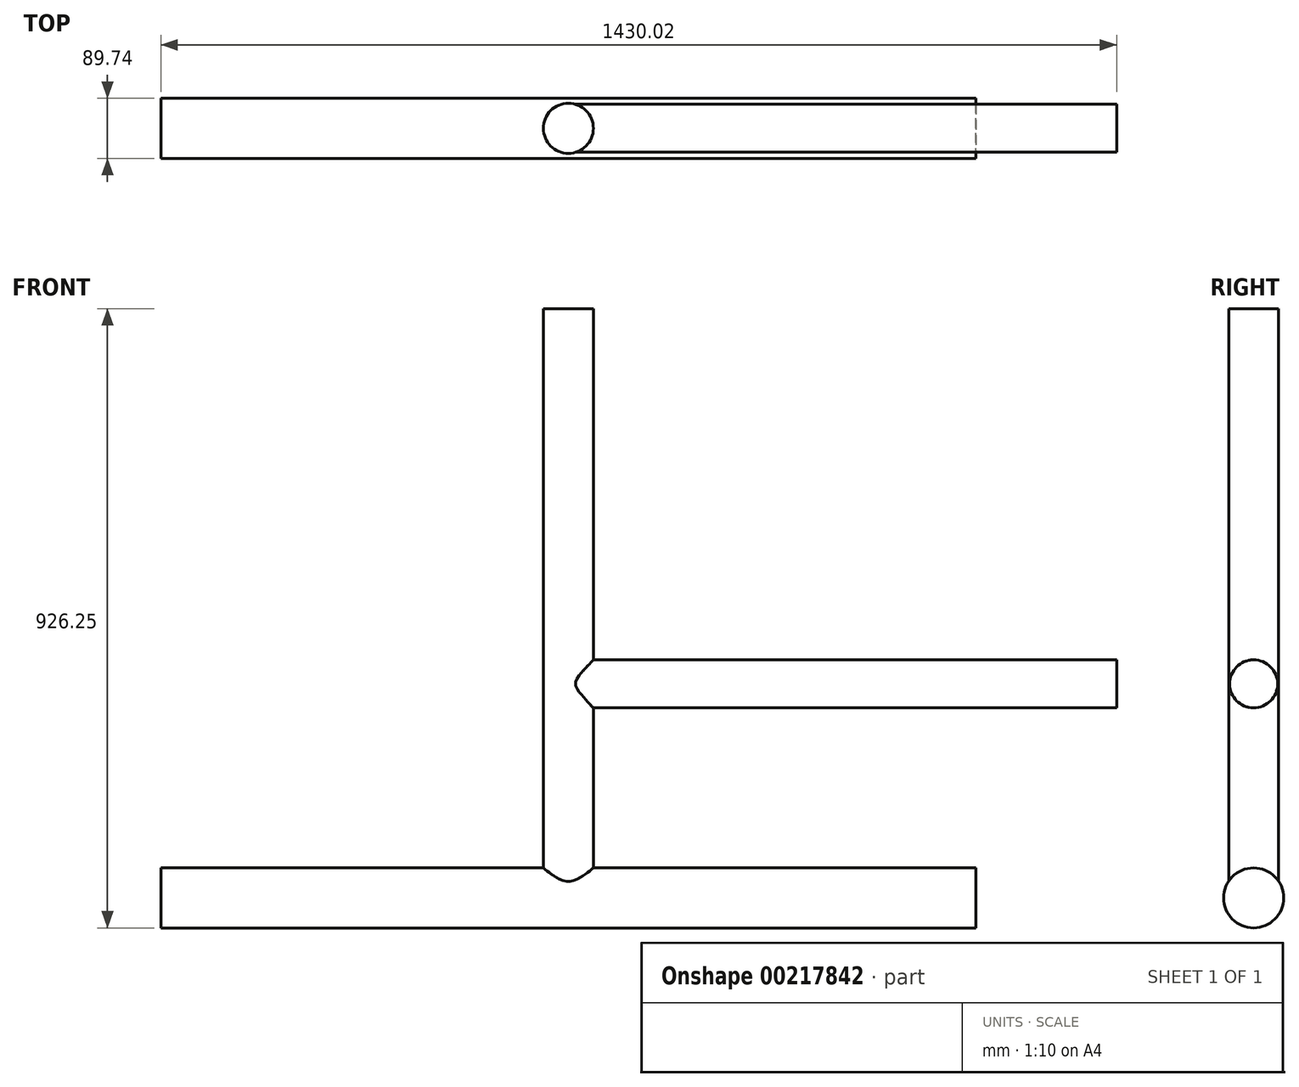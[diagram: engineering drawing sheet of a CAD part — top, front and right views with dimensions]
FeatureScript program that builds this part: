
annotation { "Feature Type Name" : "Feature", "Feature Type Description" : "" }
export const myFeature = defineFeature(function(context is Context, id is Id, definition is map)
    precondition{}
    {
        {
            var Q0;
            Q0=qCreatedBy(makeId("Top.planeOp"),FACE);
            var sketch = newSketch(context, id + "F0", { "sketchPlane" : qUnion([Q0])});
            skCircle(sketch, "E0", {"center": v(0, 0) * mm, "radius": 23.13 * mm});
            skSolve(sketch);
        }
        {
            var Q0;
            Q0 = qSketchRegion(id + "F0", true);
            extrude(context, id + "F1", {"entities" : qUnion([Q0]), "depth" : 711.2 * mm});
        }
        {
            var Q0;
            Q0=qCreatedBy(makeId("Right.planeOp"),FACE);
            var sketch = newSketch(context, id + "F2", { "sketchPlane" : qUnion([Q0])});
            skCircle(sketch, "E1", {"center": v(0, 0) * mm, "radius": 44.87 * mm});
            skSolve(sketch);
        }
        {
            var Q0;
            Q0 = qSketchRegion(id + "F2", true);
            extrude(context, id + "F3", {"entities" : qUnion([Q0]), "operationType" : NewBodyOperationType.ADD, "depth" : 609.6 * mm, "hasSecondDirection" : true, "secondDirectionOppositeDirection" : true, "secondDirectionDepth" : 609.6 * mm});
        }
        {
            var Q0;
            Q0=qCreatedBy(makeId("Top.planeOp"),FACE);
            var sketch = newSketch(context, id + "F4", { "sketchPlane" : qUnion([Q0])});
            skCircle(sketch, "E2", {"center": v(0, 0) * mm, "radius": 37.42 * mm});
            skSolve(sketch);
        }
        {
            var Q0;
            Q0 = qSketchRegion(id + "F4", true);
            extrude(context, id + "F5", {"entities" : qUnion([Q0]), "operationType" : NewBodyOperationType.ADD, "depth" : 881.38 * mm});
        }
        {
            var Q0;
            Q0=qCreatedBy(makeId("Right.planeOp"),FACE);
            var sketch = newSketch(context, id + "F6", { "sketchPlane" : qUnion([Q0])});
            skCircle(sketch, "E3", {"center": v(0, 0) * mm, "radius": 42.2 * mm});
            skSolve(sketch);
        }
        {
            var Q0;
            Q0 = qSketchRegion(id + "F6", true);
            extrude(context, id + "F7", {"entities" : qUnion([Q0]), "operationType" : NewBodyOperationType.ADD, "oppositeDirection" : true, "depth" : 43.18 * mm});
        }
        {
            var Q0;
            Q0=qCreatedBy(makeId("Right.planeOp"),FACE);
            var sketch = newSketch(context, id + "F8", { "sketchPlane" : qUnion([Q0])});
            skCircle(sketch, "E4", {"center": v(0, 320.28) * mm, "radius": 35.9 * mm});
            skSolve(sketch);
        }
        {
            var Q0;
            Q0 = qSketchRegion(id + "F8", true);
            extrude(context, id + "F9", {"entities" : qUnion([Q0]), "operationType" : NewBodyOperationType.ADD, "depth" : 820.42 * mm});
        }
    });
